# Revit family: Camera-Security-iPRO-5MP-Outdoor-Bullet-Network-S15500-V3LNX
name_source: partatom
category: Security Devices
units: mm (PartAtom-declared; Revit-internal decimal feet)

## family parameters
Cut with Voids When Loaded = No
Host = Face
Maintain Annotation Orientation = No
OmniClass Number = 23.85.10.14.11
OmniClass Title = Cameras
Part Type = Normal
Room Calculation Point = No
Round Connector Dimension = Use Diameter
Shared = No

## types (1)
- WV-S15500-V3LN
    5MP = Resolution : 5MP
    Alarm Input Or Output Specification = ALARM IN 1 (Alarm input 1/ Black & white input/ Auto time adjustment input) (x1) ALARM IN 2 (Alarm input 2/ ALARM OUT) (x1) ALARM IN 3 (Alarm input 3/ AUX OUT) (x1)
    Angle Of View = 106
    Audio In = Yes
    Audio Out = Yes
    Black Material = Metal - iPRO - Black
    Communication Ports = 10Base-T / 100Base-TX, RJ45 connector
    Date Last Modified = 2022/08/03
    Day Or Night = Yes
    Default Elevation = 0 "
    Depth = 15.07874 "
    Description = Security Camera, 5Mega Pixel, Outdoor, Bullet Network Camera WV-S15500-V3LN
    Equipment Abbreviation = SC
    Family Version = 1.0.0
    Full HD = Resolution : Full HD
    HD = Resolution : HD
    HFOV Max 169 = 106.00°
    HFOV Max 43 = 106.00°
    HFOV Min 169 = 34.00°
    HFOV Min 43 = 34.00°
    Has POE = Yes
    Height = 5.23622 "
    IP Or Analog = IP
    Indoor Or Outdoor = Outdoor
    Manufacturer = i-PRO Co., Ltd.
    Minimum Illumination = 0.050 lx
    Model = WV-S15500-V3LN
    Model Disclaimer = Contact i-Pro for more information
    Mounting Positions = Mount Dependent or Surface Mount
    Operational Humidity = 10 to 100 % (no condensation)
    Operational Temperature = -40 °C to +60 °C (-40 °F to 140 °F)
    Panning Range = On Ceiling : -180 to +180, On Wall : -100 to +100
    Part Description = Security Camera, 5Mega Pixel, Outdoor, Bullet Network Camera WV-S15500-V3LN
    Part Number = WV-S15500-V3LN
    Product Documentation Link = https://bizpartner.panasonic.net
    Product Material = Paint - i-Pro White
    Product Page URL = https://i-pro.com
    Provide Feedback = https://i-pro.com
    Regulatory Compliance = UL (UL62368-1), c-UL (CSA C22.2 No.62368-1), CE, IEC62368-1,FCC (Part15 ClassA), ICES-003 ClassA, EN55032 ClassA, EN55035
    Shock Resistance = IK10 (IEC 62262)
    Storage Temperature = -40 °C to +60 °C (-40 °F to 140 °F)
    Super Dynamic Range = Yes
    Tilting Range = On Ceiling : 0 to +100. On Wall : -100 to +100
    URL = https://i-pro.com
    VFOV Max 169 = 57.00°
    VFOV Max 43 = 77.00°
    VFOV Min 169 = 19.00°
    VFOV Min 43 = 25.00°
    Vandal Resistant = Yes
    WQHD = Resolution : WQHD
    Water and Dust Resistance = IP66, IEC60529 measuring standard compatible, Type 4X(UL50E), NEMA 4X compliant
    Width = 5.23622 "
    Yaw Max = 100.00°
    Yaw Min = -190.00°
    Yawing Range = -190 to +100
    z Camera Center Offset = 0.2874 "
    z Camera Center Offset Base = 1.1811 "
    z Column Height = 3.11024 "
    z Const CameraYawAxis = 15.74803 "
    z Const Pan Handle Length = 27.55906 "
    z Const Tilt Base Length = 9.84252 "
    z Const Tilt Base2 Length = 19.68504 "
    z Const Tilt Handle Length = 14.17323 "
    z Const Yaw Axis Length = 7.87402 "
    z Const Yaw Base Length = 10.23622 "
    z Const Yaw Base2 Length = 17.32283 "
    z Const Yaw Handle Length = 9.25197 "
    z Hinge Height = 4.56693 "
    z VV Viewpoint Depth Max = 8.54331 "
    z VV Viewpoint Depth Min = 8.54331 "

## geometry (parser evidence)
native form markers: Blend x2, Sweep x9
no freeform markers — native parametric forms only
